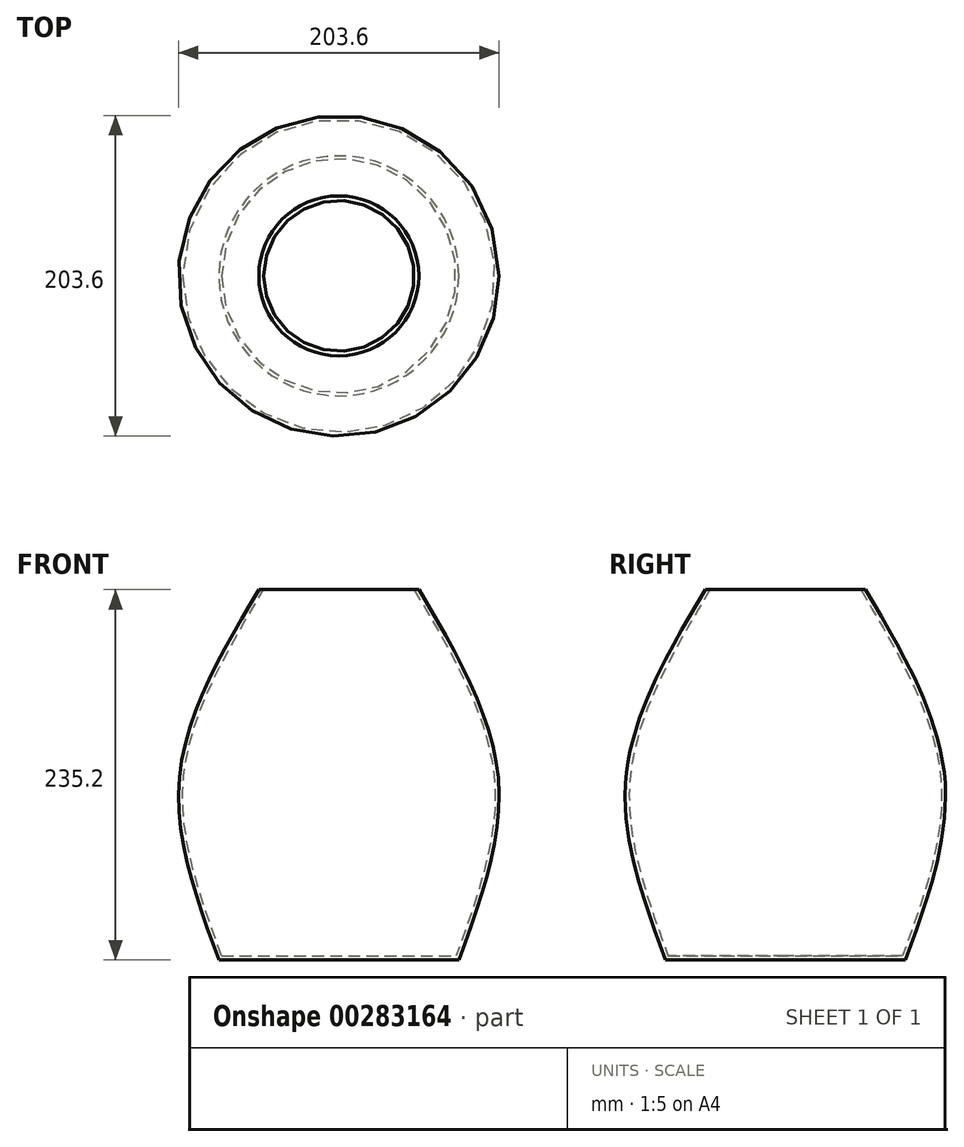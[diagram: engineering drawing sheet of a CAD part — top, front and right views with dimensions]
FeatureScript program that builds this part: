
annotation { "Feature Type Name" : "Feature", "Feature Type Description" : "" }
export const myFeature = defineFeature(function(context is Context, id is Id, definition is map)
    precondition{}
    {
        {
            var Q0;
            Q0=qCreatedBy(makeId("Top.planeOp"),FACE);
            var sketch = newSketch(context, id + "F0", { "sketchPlane" : qUnion([Q0])});
            skCircle(sketch, "E0", {"center": v(0, 0) * mm, "radius": 76.2 * mm});
            skSolve(sketch);
        }
        {
            var Q0;
            Q0=qCreatedBy(makeId("Top.planeOp"),FACE);
            cPlane(context, id + "F1", {"entities" : qUnion([Q0]), "cplaneType" : CPlaneType.OFFSET, "offset" : 111 * mm, "width" : 152.4 * mm, "height" : 152.4 * mm});
        }
        {
            var Q0;
            Q0=qCreatedBy(id+"F1.planeOp",FACE);
            var sketch = newSketch(context, id + "F2", { "sketchPlane" : qUnion([Q0])});
            skCircle(sketch, "E1", {"center": v(0, 0) * mm, "radius": 101.6 * mm});
            skSolve(sketch);
        }
        {
            var Q0;
            Q0=qCreatedBy(id+"F1.planeOp",FACE);
            cPlane(context, id + "F3", {"entities" : qUnion([Q0]), "cplaneType" : CPlaneType.OFFSET, "offset" : 124.2 * mm, "width" : 152.4 * mm, "height" : 152.4 * mm});
        }
        {
            var Q0;
            Q0=qCreatedBy(id+"F3.planeOp",FACE);
            var sketch = newSketch(context, id + "F4", { "sketchPlane" : qUnion([Q0])});
            skCircle(sketch, "E2", {"center": v(0, 0) * mm, "radius": 50.8 * mm});
            skSolve(sketch);
        }
        {
            var Q0;
            Q0=makeQuery(id+"F0.imprint","IMPRINT",FACE,{"disambiguationData":[TD([[makeQuery(id+"F0.imprint","IMPRINT",EDGE,{"derivedFrom":sQuery(id+"F0.wireOp",EDGE,"E0")}),1.0]])]});
            var Q1;
            Q1=makeQuery(id+"F2.imprint","IMPRINT",FACE,{"disambiguationData":[TD([[makeQuery(id+"F2.imprint","IMPRINT",EDGE,{"derivedFrom":sQuery(id+"F2.wireOp",EDGE,"E1")}),1.0]])]});
            var Q2;
            Q2=makeQuery(id+"F4.imprint","IMPRINT",FACE,{"disambiguationData":[TD([[makeQuery(id+"F4.imprint","IMPRINT",EDGE,{"derivedFrom":sQuery(id+"F4.wireOp",EDGE,"E2")}),1.0]])]});
            loft(context, id + "F5", {"sheetProfilesArray" : [{ "sheetProfileEntities" : qUnion([Q0]) }, { "sheetProfileEntities" : qUnion([Q1]) }, { "sheetProfileEntities" : qUnion([Q2]) }]});
        }
        {
            var Q0;
            Q0=makeQuery(id+"F5.opLoft","CAP_FACE",FACE,{"disambiguationData":[OSD([makeQuery(id+"F4.imprint","IMPRINT",FACE,{"disambiguationData":[TD([[makeQuery(id+"F4.imprint","IMPRINT",EDGE,{"derivedFrom":sQuery(id+"F4.wireOp",EDGE,"E2")}),1.0]])]})])],"isStart":true});
            shell(context, id + "F6", {"entities" : qUnion([Q0]), "thickness" : 2.54 * mm});
        }
    });
